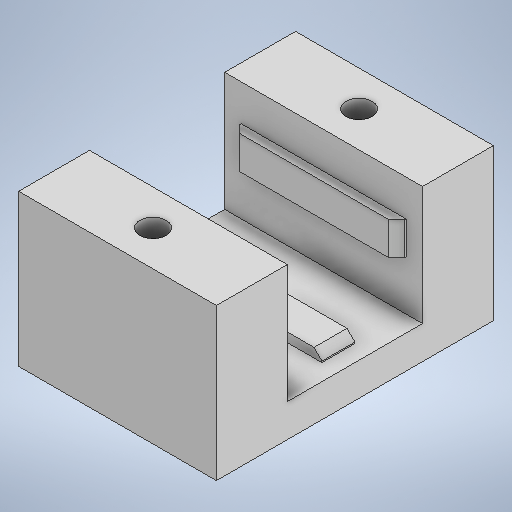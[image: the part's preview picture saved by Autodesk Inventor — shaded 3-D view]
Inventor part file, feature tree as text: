
AUTODESK INVENTOR PART (.ipt)
format: ipt  version: 2025 (Build 290162010, 162A)  size: 275,456 bytes
history: native  units: in
note: dims shown in document units (in); Inventor stores cm internally (conversion verified against a paired STEP export)
features: extrude x6, sketch x6, chamfer x2
ambient origin geometry x8: Origin, YZ Plane, XZ Plane, XY Plane, X Axis, Y Axis, Z Axis, Center Point
bodies: Body1 (feature_tree)
feature tree (14):
  extrude  "Extrusion16"  Depth=1.1811in
  extrude  "Extrusion17"  Depth=0.7087in TaperAngle=0.0deg
  extrude  "Extrusion18"  Depth=0.2953in
  extrude  "Extrusion19"  Depth=0.9843in
  extrude  "Extrusion20"  Depth=0.0551in TaperAngle=0.0deg
  chamfer  "Fasen4"  Distance=0.0551in
  extrude  "Extrusion21"  Depth=0.0551in TaperAngle=0.0deg
  chamfer  "Fasen5"  Distance=0.0787in Angle=45.0deg
  sketch  "Skizze16"  dims[d82=1.6535in d83=1.1811in]
  sketch  "Skizze17"  dims[d84=0.1969in d85=0.0in d89=0.7087in d90=0.0in]
  sketch  "Skizze19"  dims[d91=0.8071in d92=0.2953in]
  sketch  "Skizze20"  dims[d93=0.1969in d94=0.9843in]
  sketch  "Skizze21"  dims[d95=0.5906in d96=0.0551in d97=0.0in d98=0.0551in d99=0.0in]
  sketch  "Skizze22"  dims[d100=0.1969in d101=0.0551in d102=0.0in d103=0.0472in d104=0.0787in d105=45.0deg d106=0.1575in d107=0.2116in d108=0.0in d109=0.0in d110=0.1181in d111=0.0787in d112=45.0deg d37=0.0197in d38=0.0344in d39=0.0197in d40=0.0344in d41=0.0197in d42=0.0344in]
